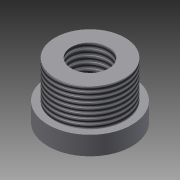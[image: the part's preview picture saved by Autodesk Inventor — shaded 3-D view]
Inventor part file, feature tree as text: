
AUTODESK INVENTOR PART (.ipt)
format: ipt  version: 2013 (Build 170138000, 138)  size: 100,352 bytes
history: native  units: in
note: dims shown in document units (in); Inventor stores cm internally (conversion verified against a paired STEP export)
features: extrude x2, thread x2, sketch x2
ambient origin geometry x8: Origin, YZ Plane, XZ Plane, XY Plane, X Axis, Y Axis, Z Axis, Center Point
bodies: Solid1 (feature_tree)
feature tree (6):
  extrude  "Extrusion1"  Depth=1.12in
  extrude  "Extrusion2"  Depth=0.937in
  thread  "Thread3"  [1 undecoded]
  thread  "Thread4"  [1 undecoded]
  sketch  "Sketch1"  dims[d0=0.5in d1=1.12in]
  sketch  "Sketch2"  dims[d2=0.75in d3=0.0in d6=0.937in d8=0.5in d9=0.0in d14=0.782in d15=0.0in d16=1.0in d17=0.0in]
note: 2 required parameter values undecoded (feature->parameter linkage not recoverable at this tier; creation-order binding heuristic only, values carry confidence <= 0.55)
